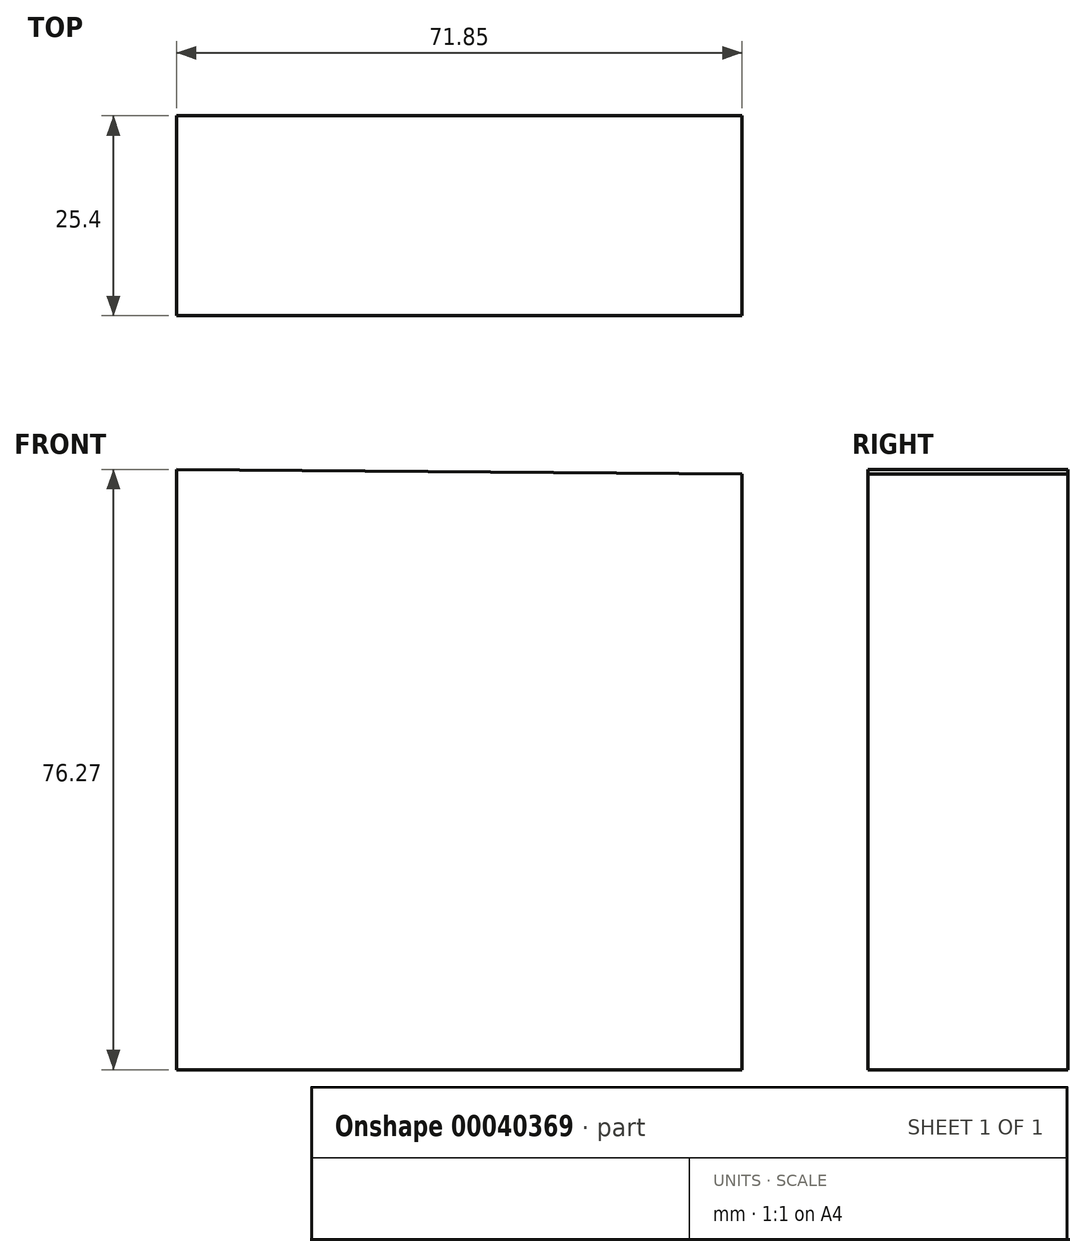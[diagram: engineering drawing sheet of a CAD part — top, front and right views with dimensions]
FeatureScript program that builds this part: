
annotation { "Feature Type Name" : "Feature", "Feature Type Description" : "" }
export const myFeature = defineFeature(function(context is Context, id is Id, definition is map)
    precondition{}
    {
        {
            var Q0;
            Q0=qCreatedBy(makeId("Front.planeOp"),FACE);
            var sketch = newSketch(context, id + "F0", { "sketchPlane" : qUnion([Q0])});
            skLineSegment(sketch, "E0", {"start": v(-39.37, 76.27) * mm, "end": v(-39.37, 0) * mm});
            skLineSegment(sketch, "E1", {"start": v(-39.37, 0) * mm, "end": v(32.48, 0) * mm});
            skLineSegment(sketch, "E2", {"start": v(32.48, 0) * mm, "end": v(32.48, 75.68) * mm});
            skLineSegment(sketch, "E3", {"start": v(-39.37, 76.27) * mm, "end": v(32.48, 75.68) * mm});
            skLineSegment(sketch, "E4", {"start": v(-39.37, 0) * mm, "end": v(-76.37, -56.4) * mm});
            skLineSegment(sketch, "E5", {"start": v(-76.37, -56.4) * mm, "end": v(0, -56.4) * mm});
            skLineSegment(sketch, "E6", {"start": v(0, -56.4) * mm, "end": v(75.78, -56.4) * mm});
            skLineSegment(sketch, "E7", {"start": v(75.78, -56.4) * mm, "end": v(32.48, 0) * mm});
            skSolve(sketch);
        }
        {
            var Q0;
            Q0=makeQuery(id+"F0.imprint","IMPRINT",FACE,{"disambiguationData":[TD([[makeQuery(id+"F0.imprint","IMPRINT",EDGE,{"derivedFrom":sQuery(id+"F0.wireOp",EDGE,"E0")}),1.0]])]});
            extrude(context, id + "F1", {"entities" : qUnion([Q0]), "depth" : 25.4 * mm});
        }
    });
